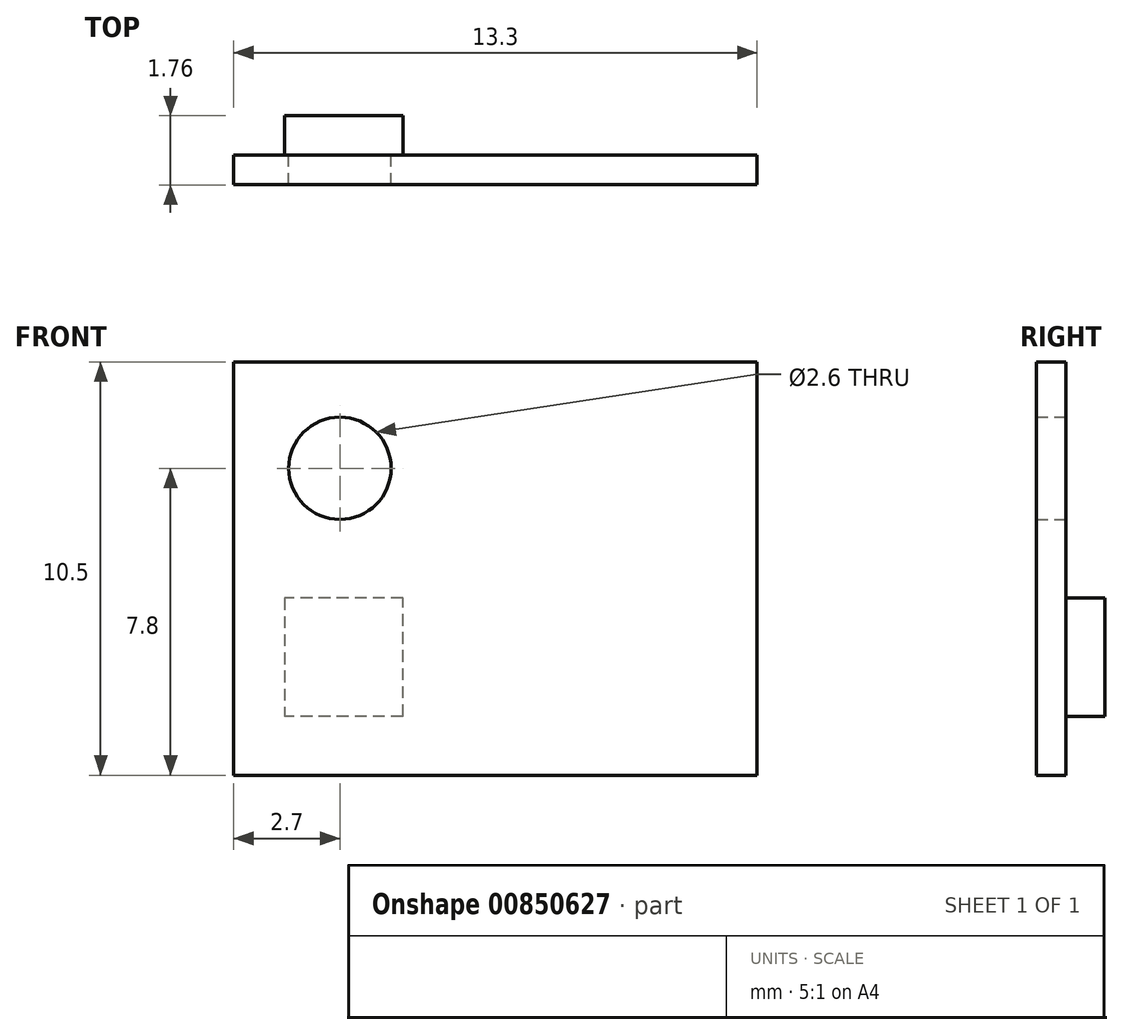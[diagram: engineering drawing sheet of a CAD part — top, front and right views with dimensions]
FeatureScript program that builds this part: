
annotation { "Feature Type Name" : "Feature", "Feature Type Description" : "" }
export const myFeature = defineFeature(function(context is Context, id is Id, definition is map)
    precondition{}
    {
        {
            var Q0;
            Q0=qCreatedBy(makeId("Front.planeOp"),FACE);
            var sketch = newSketch(context, id + "F0", { "sketchPlane" : qUnion([Q0])});
            skLineSegment(sketch, "E0.top", {"start": v(6.65, 5.25) * mm, "end": v(-6.65, 5.25) * mm});
            skLineSegment(sketch, "E0.left", {"start": v(6.65, -5.25) * mm, "end": v(6.65, 5.25) * mm});
            skLineSegment(sketch, "E0.right", {"start": v(-6.65, -5.25) * mm, "end": v(-6.65, 5.25) * mm});
            skPoint(sketch, "E0.middle", {"position": v(0, 0) * mm});
            skLineSegment(sketch, "E1", {"start": v(-6.65, 5.25) * mm, "end": v(-3.95, 5.25) * mm});
            skLineSegment(sketch, "E2", {"start": v(-3.95, 5.25) * mm, "end": v(-3.95, 2.55) * mm});
            skCircle(sketch, "E3", {"center": v(-3.95, 2.55) * mm, "radius": 1.3 * mm});
            skLineSegment(sketch, "E4", {"start": v(-6.65, -5.25) * mm, "end": v(6.65, -5.25) * mm});
            skSolve(sketch);
        }
        {
            var Q0;
            Q0=makeQuery(id+"F0.imprint","IMPRINT",FACE,{"disambiguationData":[TD([[makeQuery(id+"F0.imprint","IMPRINT",EDGE,{"derivedFrom":sQuery(id+"F0.wireOp",EDGE,"E0.top")}),1.0]])]});
            extrude(context, id + "F1", {"entities" : qUnion([Q0]), "endBound" : BoundingType.SYMMETRIC, "depth" : 0.75 * mm, "offsetDistance" : 25 * mm});
        }
        {
            var Q0;
            Q0=makeQuery(id+"F1.opExtrude","CAP_FACE",FACE,{"disambiguationData":[OSD([sQuery(id+"F0.wireOp",EDGE,"E0.top"),sQuery(id+"F0.wireOp",EDGE,"E0.left"),sQuery(id+"F0.wireOp",EDGE,"E0.right"),sQuery(id+"F0.wireOp",EDGE,"E1"),sQuery(id+"F0.wireOp",EDGE,"E3"),sQuery(id+"F0.wireOp",EDGE,"E4")])],"isStart":true});
            var sketch = newSketch(context, id + "F2", { "sketchPlane" : qUnion([Q0])});
            skLineSegment(sketch, "E5", {"start": v(6.65, -5.25) * mm, "end": v(2.35, -5.25) * mm});
            skLineSegment(sketch, "E6", {"start": v(2.35, -5.25) * mm, "end": v(2.35, -0.75) * mm});
            skLineSegment(sketch, "E7.bottom", {"start": v(2.35, -0.75) * mm, "end": v(5.35, -0.75) * mm});
            skLineSegment(sketch, "E7.top", {"start": v(2.35, -3.75) * mm, "end": v(5.35, -3.75) * mm});
            skLineSegment(sketch, "E7.left", {"start": v(2.35, -0.75) * mm, "end": v(2.35, -3.75) * mm});
            skLineSegment(sketch, "E7.right", {"start": v(5.35, -0.75) * mm, "end": v(5.35, -3.75) * mm});
            skSolve(sketch);
        }
        {
            var Q0;
            Q0=makeQuery(id+"F2.imprint","IMPRINT",FACE,{"disambiguationData":[TD([[makeQuery(id+"F2.imprint","IMPRINT",EDGE,{"derivedFrom":sQuery(id+"F2.wireOp",EDGE,"E7.bottom")}),-1.0]])]});
            extrude(context, id + "F3", {"entities" : qUnion([Q0]), "operationType" : NewBodyOperationType.ADD, "depth" : 1 * mm, "offsetDistance" : 25 * mm});
        }
    });
